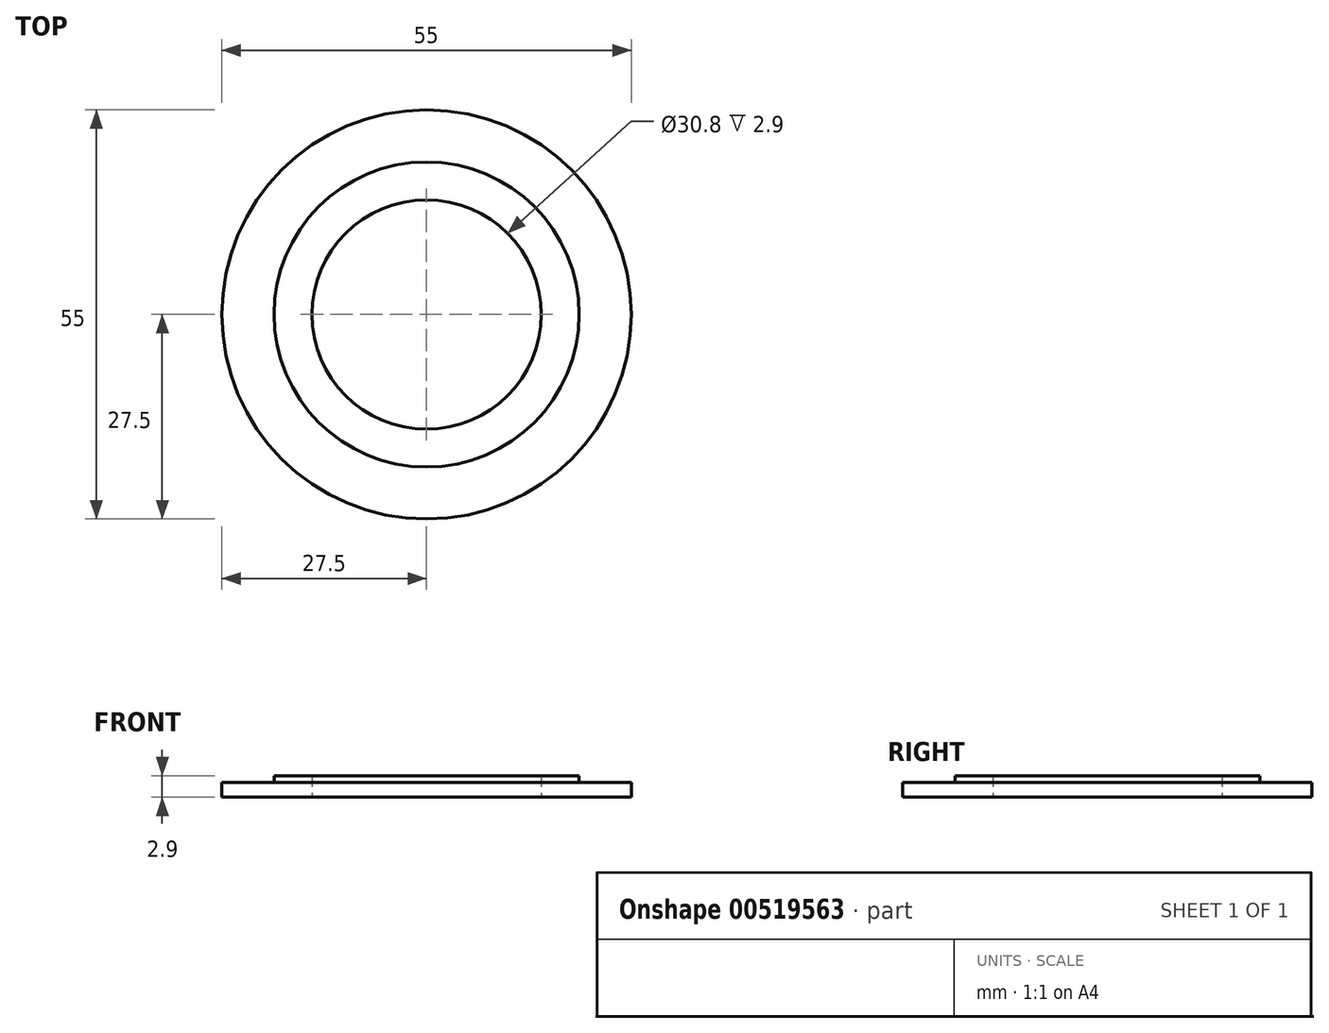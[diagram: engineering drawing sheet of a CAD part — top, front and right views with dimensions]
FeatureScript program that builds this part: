
annotation { "Feature Type Name" : "Feature", "Feature Type Description" : "" }
export const myFeature = defineFeature(function(context is Context, id is Id, definition is map)
    precondition{}
    {
        {
            var Q0;
            Q0=qCreatedBy(makeId("Top.planeOp"),FACE);
            var sketch = newSketch(context, id + "F0", { "sketchPlane" : qUnion([Q0])});
            skCircle(sketch, "E0", {"center": v(0, 0) * mm, "radius": 27.5 * mm});
            skCircle(sketch, "E1", {"center": v(0, 0) * mm, "radius": 15.4 * mm});
            skSolve(sketch);
        }
        {
            var Q0;
            Q0=makeQuery(id+"F0.imprint","IMPRINT",FACE,{"disambiguationData":[TD([[makeQuery(id+"F0.imprint","IMPRINT",EDGE,{"derivedFrom":sQuery(id+"F0.wireOp",EDGE,"E0")}),1.0]])]});
            extrude(context, id + "F1", {"entities" : qUnion([Q0]), "depth" : 2 * mm, "offsetDistance" : 25 * mm});
        }
        {
            var Q0;
            Q0=makeQuery(id+"F1.opExtrude","CAP_FACE",FACE,{"disambiguationData":[OSD([sQuery(id+"F0.wireOp",EDGE,"E0"),sQuery(id+"F0.wireOp",EDGE,"E1")])],"isStart":false});
            var sketch = newSketch(context, id + "F2", { "sketchPlane" : qUnion([Q0])});
            skCircle(sketch, "E2", {"center": v(0, 0) * mm, "radius": 20.5 * mm});
            skCircle(sketch, "E3", {"center": v(0, 0) * mm, "radius": 15.4 * mm});
            skSolve(sketch);
        }
        {
            var Q0;
            Q0=makeQuery(id+"F2.imprint","IMPRINT",FACE,{"disambiguationData":[TD([[makeQuery(id+"F2.imprint","IMPRINT",EDGE,{"derivedFrom":sQuery(id+"F2.wireOp",EDGE,"E2")}),1.0]])]});
            extrude(context, id + "F3", {"entities" : qUnion([Q0]), "operationType" : NewBodyOperationType.ADD, "depth" : .9 * mm, "offsetDistance" : 25 * mm});
        }
    });
